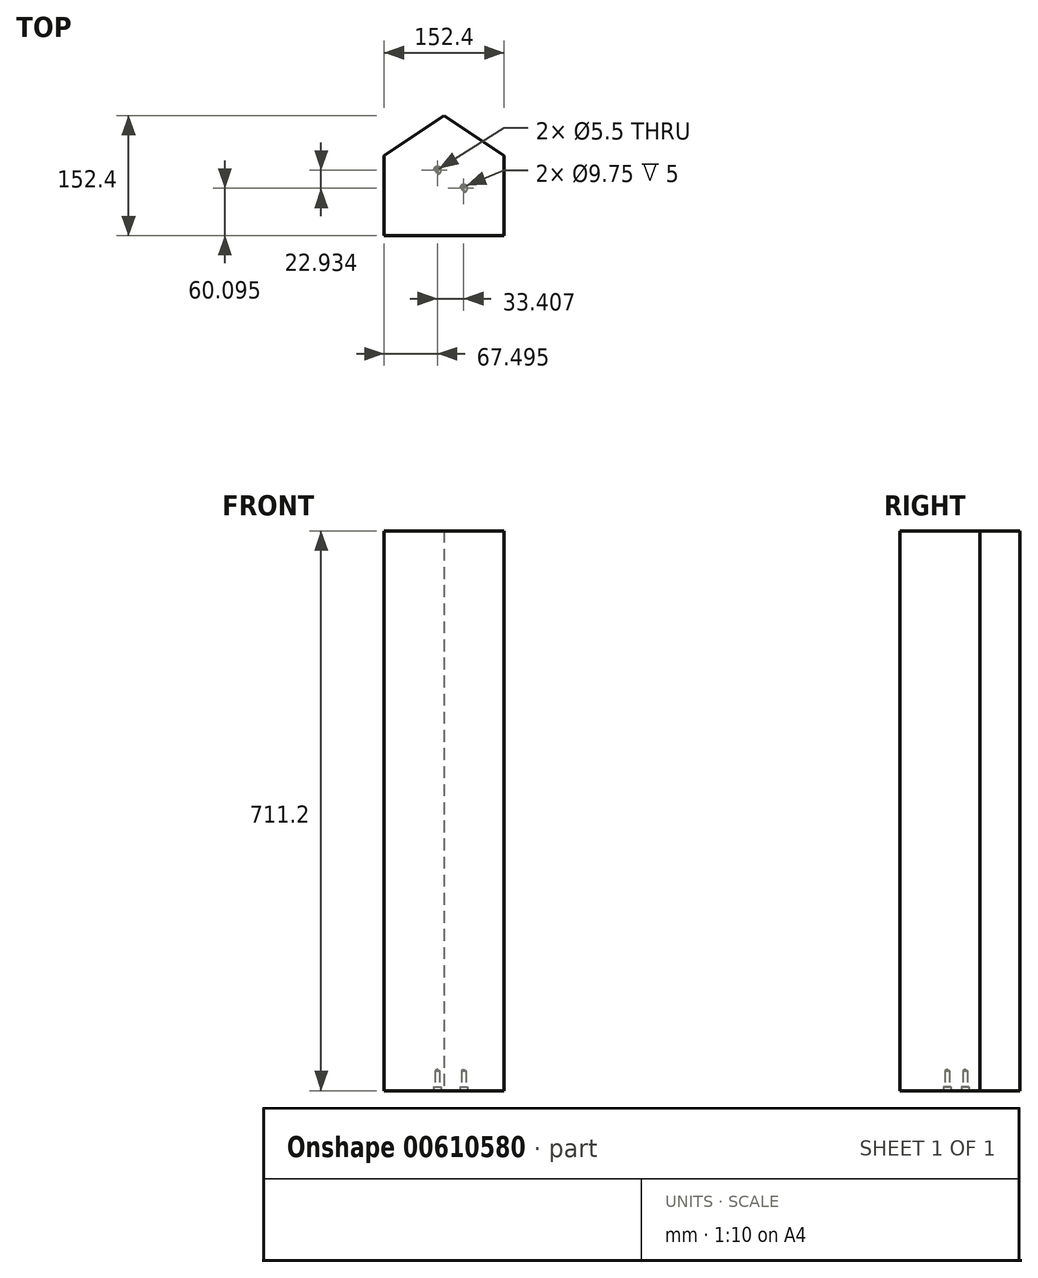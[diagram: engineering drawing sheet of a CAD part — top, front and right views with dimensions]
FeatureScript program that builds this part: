
annotation { "Feature Type Name" : "Feature", "Feature Type Description" : "" }
export const myFeature = defineFeature(function(context is Context, id is Id, definition is map)
    precondition{}
    {
        {
            var Q0;
            Q0=qCreatedBy(makeId("Top.planeOp"),FACE);
            var sketch = newSketch(context, id + "F0", { "sketchPlane" : qUnion([Q0])});
            skLineSegment(sketch, "E0", {"start": v(0, 0) * mm, "end": v(152.4, 0) * mm});
            skLineSegment(sketch, "E1", {"start": v(152.4, 0) * mm, "end": v(152.4, 101.6) * mm});
            skLineSegment(sketch, "E2", {"start": v(152.4, 101.6) * mm, "end": v(76.2, 152.4) * mm});
            skLineSegment(sketch, "E3", {"start": v(76.2, 152.4) * mm, "end": v(0, 101.6) * mm});
            skLineSegment(sketch, "E4", {"start": v(0, 101.6) * mm, "end": v(0, 0) * mm});
            skLineSegment(sketch, "E5", {"start": v(76.2, 152.4) * mm, "end": v(76.2, 0) * mm, "construction": true});
            skSolve(sketch);
        }
        {
            var Q0;
            Q0=makeQuery(id+"F0.imprint","IMPRINT",FACE,{"disambiguationData":[TD([[makeQuery(id+"F0.imprint","IMPRINT",EDGE,{"derivedFrom":sQuery(id+"F0.wireOp",EDGE,"E0")}),1.0]])]});
            var Q1;
            Q1 = qSketchRegion(id + "FWEhPE5W8fg5KpU_1", true);
            extrude(context, id + "F1", {"entities" : qUnion([Q0, Q1]), "depth" : 711.2 * mm, "offsetDistance" : 25.4 * mm});
        }
        {
            var Q0;
            Q0=makeQuery(id+"F1.opExtrude","CAP_FACE",FACE,{"disambiguationData":[OSD([sQuery(id+"F0.wireOp",EDGE,"E0"),sQuery(id+"F0.wireOp",EDGE,"E1"),sQuery(id+"F0.wireOp",EDGE,"E2"),sQuery(id+"F0.wireOp",EDGE,"E3"),sQuery(id+"F0.wireOp",EDGE,"E4")])],"isStart":true});
            var sketch = newSketch(context, id + "F2", { "sketchPlane" : qUnion([Q0])});
            skPoint(sketch, "E6", {"position": v(100.9, -60.1) * mm});
            skPoint(sketch, "E7", {"position": v(67.5, -83.03) * mm});
            skSolve(sketch);
        }
        {
            var Q0;
            Q0=sQuery(id+"F2.wireOp",VERTEX,"E6");
            var Q1;
            Q1=sQuery(id+"F2.wireOp",VERTEX,"E7");
            var Q2;
            Q2=makeQuery(id+"F1.opExtrude","SWEPT_BODY",BODY,{"disambiguationData":[OSD([sQuery(id+"F0.wireOp",EDGE,"E0"),sQuery(id+"F0.wireOp",EDGE,"E1"),sQuery(id+"F0.wireOp",EDGE,"E2"),sQuery(id+"F0.wireOp",EDGE,"E3"),sQuery(id+"F0.wireOp",EDGE,"E4")])]});
            hole(context, id + "F3", {"style" : HoleStyle.C_BORE, "endStyle" : HoleEndStyle.BLIND, "standardTappedOrClearance" : lookupTablePath({ "standard" : "ISO", "fit" : "Normal", "size" : "M5", "type" : "Clearance" }), "standardBlindInLast" : lookupTablePath({ "fit" : "Standard", "standard" : "ISO", "size" : "M5", "type" : "Clearance" }), "holeDiameter" : 5.5 * mm, "cBoreDiameter" : 9.75 * mm, "cBoreDepth" : 5 * mm, "majorDiameter" : 6.35 * mm, "holeDepth" : 25.4 * mm, "isTappedThrough" : true, "tappedDepth" : 12.7 * mm, "tapClearance" : 3, "locations" : qUnion([Q0, Q1]), "scope" : qUnion([Q2])});
        }
        {
            var Q0;
            Q0=makeQuery(id+"F1.opExtrude","CAP_EDGE",EDGE,{"disambiguationData":[OSD([sQuery(id+"F0.wireOp",EDGE,"E4")])],"isStart":true});
            var Q1;
            Q1=makeQuery(id+"F1.opExtrude","CAP_VERTEX",VERTEX,{"disambiguationData":[OSD([sQuery(id+"F0.wireOp",EDGE,"E3"),sQuery(id+"F0.wireOp",EDGE,"E4")])],"isStart":true});
            cPlane(context, id + "F4", {"entities" : qUnion([Q0, Q1]), "cplaneType" : CPlaneType.LINE_POINT, "offset" : 25.4 * mm, "width" : 152.4 * mm, "height" : 152.4 * mm});
        }
        {
            var Q0;
            Q0=makeQuery(id+"F1.opExtrude","CAP_FACE",FACE,{"disambiguationData":[OSD([sQuery(id+"F0.wireOp",EDGE,"E0"),sQuery(id+"F0.wireOp",EDGE,"E1"),sQuery(id+"F0.wireOp",EDGE,"E2"),sQuery(id+"F0.wireOp",EDGE,"E3"),sQuery(id+"F0.wireOp",EDGE,"E4")])],"isStart":true});
            var sketch = newSketch(context, id + "F5", { "sketchPlane" : qUnion([Q0])});
            skSolve(sketch);
        }
        {
            var Q0;
            Q0=qCreatedBy(id+"F4.planeOp",FACE);
            var sketch = newSketch(context, id + "F6", { "sketchPlane" : qUnion([Q0])});
            skSolve(sketch);
        }
        {
            var Q0;
            Q0=makeQuery(id+"F1.opExtrude","CAP_FACE",FACE,{"disambiguationData":[OSD([sQuery(id+"F0.wireOp",EDGE,"E0"),sQuery(id+"F0.wireOp",EDGE,"E1"),sQuery(id+"F0.wireOp",EDGE,"E2"),sQuery(id+"F0.wireOp",EDGE,"E3"),sQuery(id+"F0.wireOp",EDGE,"E4")])],"isStart":false});
            var sketch = newSketch(context, id + "F7", { "sketchPlane" : qUnion([Q0])});
            skPoint(sketch, "E8", {"position": v(79.09, 86.03) * mm});
            skSolve(sketch);
        }
    });
